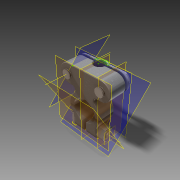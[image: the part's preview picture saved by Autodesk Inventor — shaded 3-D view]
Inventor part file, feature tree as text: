
AUTODESK INVENTOR PART (.ipt)
format: ipt  version: 2014 (Build 180170000, 170)  size: 774,656 bytes
history: native  units: in
note: dims shown in document units (in); Inventor stores cm internally (conversion verified against a paired STEP export)
features: sketch x15, projected_geometry x11, extrude x10, fillet x8, plane x8, revolve x4, other x4, thread x4, mirror x2, hole x1, chamfer x1, surface_op x1, reference x1
ambient origin geometry x8: Origin, YZ Plane, XZ Plane, XY Plane, X Axis, Y Axis, Z Axis, Center Point
bodies: Solid1 (feature_tree), Solid2 (feature_tree), Solid3 (feature_tree), Solid4 (feature_tree), Solid5 (feature_tree)
feature tree (70):
  extrude  "Extrusion1"  Depth=0.125in
  fillet  "Fillet1"  Radius=0.25in
  hole  "Hole1"  [1 undecoded]
  revolve  "Revolution1"  [1 undecoded]
  plane  "Work Plane1"
  extrude  "Extrusion2"  Depth=0.315in
  extrude  "Extrusion3"  Depth=0.0625in
  sketch  "Sketch6"  dims[d18=90.0deg d19=0.0625in]
  extrude  "Extrusion4"  Depth=0.0625in TaperAngle=0.0deg
  extrude  "Extrusion5"  Depth=0.0625in TaperAngle=0.0deg
  extrude  "Extrusion6"  TaperAngle=90.0deg  [1 undecoded]
  plane  "Work Plane2"
  sketch  "Sketch8"  dims[d24=0.0625in d25=0.0in d26=0.0625in d27=0.0in]
  other  "Work Axis1"
  revolve  "Revolution2"  [1 undecoded]
  fillet  "Fillet2"  Radius=0.2in
  fillet  "Fillet3"  [1 undecoded]
  extrude  "Extrusion7"  Depth=0.2in TaperAngle=0.0deg
  plane  "Work Plane3"
  revolve  "Revolution3"  Angle=45.0deg
  plane  "Work Plane4"
  mirror  "Mirror1"
  plane  "Work Plane5"
  extrude  "Extrusion8"  Depth=0.1375in TaperAngle=0.0deg
  thread  "Thread1"  [1 undecoded]
  chamfer  "Chamfer1"  Distance=0.01in
  thread  "Thread2"  [1 undecoded]
  thread  "Thread3"  [1 undecoded]
  extrude  "Extrusion9"  Depth=0.02in TaperAngle=0.0deg
  plane  "Work Plane6"
  sketch  "Sketch14"  dims[d50=90.0deg]
  other  "Work Axis2"
  revolve  "Revolution4"  [1 undecoded]
  fillet  "Fillet4"  Radius=0.02in
  fillet  "Fillet5"  Radius=0.02in
  plane  "Work Plane7"
  extrude  "Extrusion10"  [1 undecoded]
  thread  "Thread4"  [1 undecoded]
  plane  "Work Plane8"
  mirror  "Mirror2"
  fillet  "Fillet6"  [1 undecoded]
  fillet  "Fillet7"  [1 undecoded]
  fillet  "Fillet8"  [1 undecoded]
  surface_op  "Sculpt1"
  sketch  "Sketch1"  dims[d0=0.15in d1=0.125in d3=0.25in]
  reference  "Reference1"
  sketch  "Sketch2"  dims[d4=0.25in d5=0.2in]
  projected_geometry  "Projected Loop1"
  sketch  "Sketch3"  dims[d6=0.2in d7=0.5in d8=0.0in]
  projected_geometry  "Projected Loop2"
  sketch  "Sketch4"  dims[d9=0.2in]
  projected_geometry  "Projected Loop3"
  sketch  "Sketch5"  dims[d10=0.25in d11=0.75in d12=0.375in d13=0.25in d14=0.5635in d15=1.0in d16=0.8108in d17=0.315in]
  sketch  "Sketch7"  dims[d20=0.0625in d21=0.0in d22=0.0625in d23=0.0in]
  projected_geometry  "Projected Loop5"
  sketch  "Sketch9"  dims[d28=0.15in d29=0.0in d30=90.0deg]
  projected_geometry  "Projected Loop6"
  projected_geometry  "Projected Loop7"
  sketch  "Sketch10"  dims[d31=0.02in d32=0.01in d33=0.2in d34=0.0in d35=90.0deg]
  sketch  "Sketch11"  dims[d36=0.035in d37=0.2in d38=0.0in]
  projected_geometry  "Projected Loop8"
  projected_geometry  "Projected Loop9"
  sketch  "Sketch12"  dims[d39=1.0in d40=0.0in d41=0.02in d42=0.125in d43=45.0deg]
  sketch  "Sketch13"  dims[d44=1.0in d45=0.0in d46=1.0in d47=0.0in d48=0.1375in d49=0.0in]
  projected_geometry  "Projected Loop10"
  projected_geometry  "Projected Loop11"
  sketch  "Sketch15"  dims[d51=0.01in d52=0.01in d53=0.0625in d54=0.1375in d55=0.0in d56=1.0in d57=0.0in d58=0.1in d59=0.02in d60=0.02in]
  projected_geometry  "Project Cut Edges1"
  other  "Composite1"
  other  "Srf1"
note: 14 required parameter values undecoded (feature->parameter linkage not recoverable at this tier; creation-order binding heuristic only, values carry confidence <= 0.55)